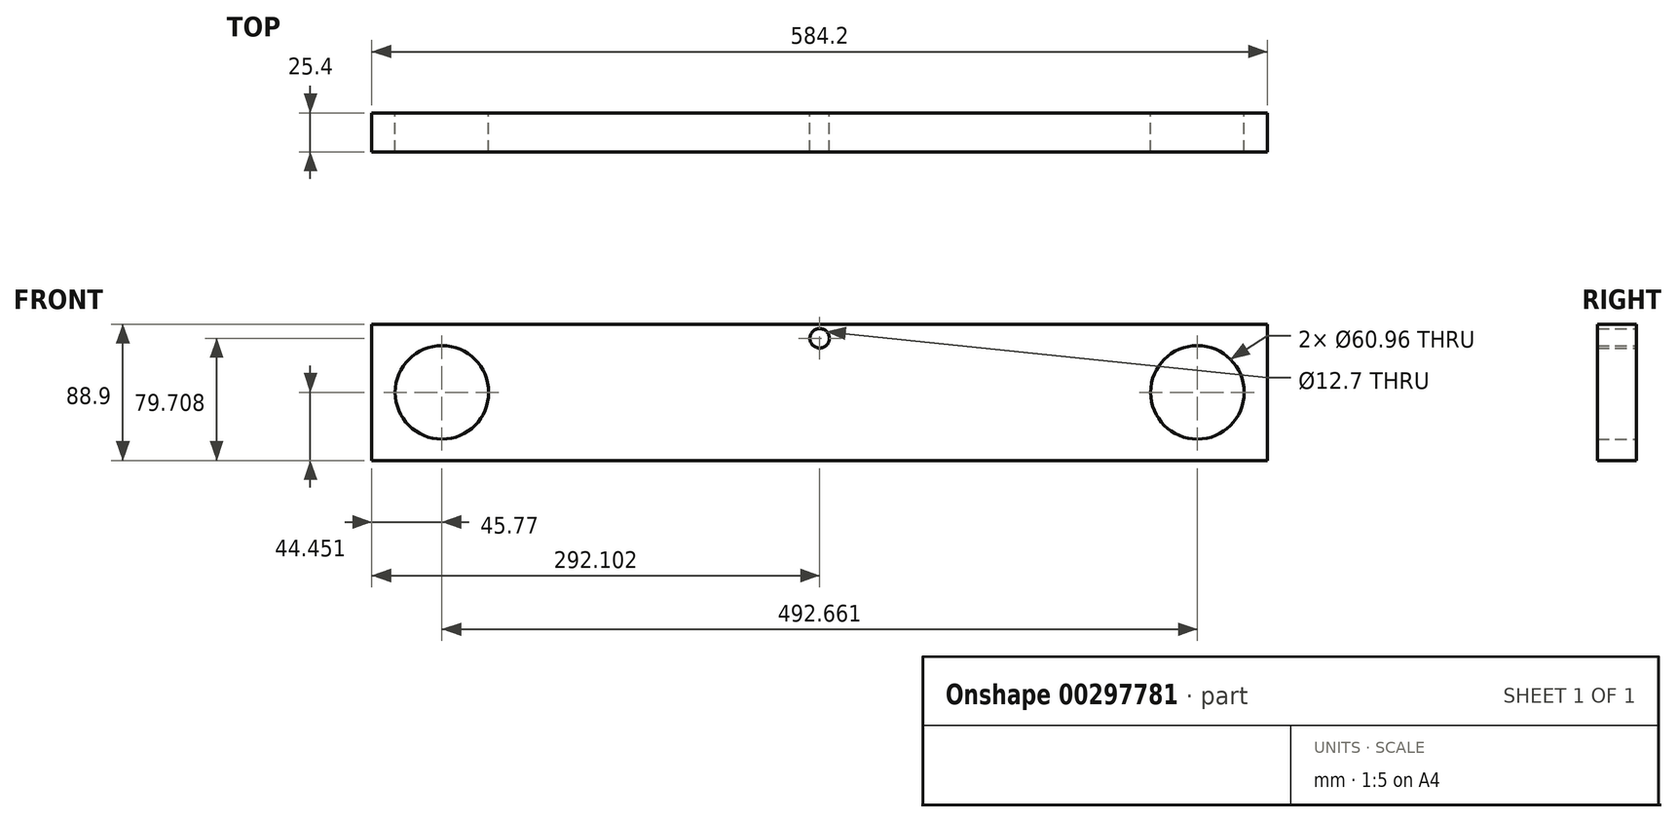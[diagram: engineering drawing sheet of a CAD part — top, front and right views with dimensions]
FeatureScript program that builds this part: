
annotation { "Feature Type Name" : "Feature", "Feature Type Description" : "" }
export const myFeature = defineFeature(function(context is Context, id is Id, definition is map)
    precondition{}
    {
        {
            var Q0;
            Q0=qCreatedBy(makeId("Front.planeOp"),FACE);
            var sketch = newSketch(context, id + "F0", { "sketchPlane" : qUnion([Q0])});
            skLineSegment(sketch, "E0.bottom", {"start": v(-315.3, 71.01) * mm, "end": v(268.9, 71.01) * mm});
            skLineSegment(sketch, "E0.top", {"start": v(-315.3, -17.89) * mm, "end": v(268.9, -17.89) * mm});
            skLineSegment(sketch, "E0.left", {"start": v(-315.3, 71.01) * mm, "end": v(-315.3, -17.89) * mm});
            skLineSegment(sketch, "E0.right", {"start": v(268.9, 71.01) * mm, "end": v(268.9, -17.89) * mm});
            skCircle(sketch, "E1", {"center": v(-269.53, 26.56) * mm, "radius": 30.48 * mm});
            skCircle(sketch, "E2", {"center": v(223.13, 26.56) * mm, "radius": 30.48 * mm});
            skPoint(sketch, "E3", {"position": v(-23.2, 71.01) * mm});
            skLineSegment(sketch, "E4", {"start": v(-23.2, 71.01) * mm, "end": v(-23.2, -17.89) * mm, "construction": true});
            skCircle(sketch, "E5", {"center": v(-23.2, 61.82) * mm, "radius": 6.35 * mm});
            skSolve(sketch);
        }
        {
            var Q0;
            Q0=makeQuery(id+"F0.imprint","IMPRINT",FACE,{"disambiguationData":[TD([[makeQuery(id+"F0.imprint","IMPRINT",EDGE,{"derivedFrom":sQuery(id+"F0.wireOp",EDGE,"E0.bottom")}),-1.0]])]});
            extrude(context, id + "F1", {"entities" : qUnion([Q0]), "depth" : 25.4 * mm});
        }
    });
